# Revit family: CVSL-WM
name_source: partatom
category: Lighting Fixtures
revit_build: Autodesk Revit 2013 (Build: 20130531_2115(x64)
units: mm (PartAtom-declared; Revit-internal decimal feet)

## types (1)
- CVSL
    Apparent Load = 63 VA
    Assembly Code = D5020210
    Color Filter = 16777215
    Description = Curvista Wall Mount
    Dimming Lamp Color Temperature Shift = <None>
    Emit Shape Visible in Rendering = No
    Emit from Rectangle Length = 3 "
    Emit from Rectangle Width = 48 "
    Glass = Hubbell - White Glass
    Housing Material = Hubbell - White
    Lamp = T5, T5HO, T8
    Load Classification = Lighting
    Manufacturer = Alera Lighting
    Model = CVSLWM
    Photometric Notes = More IES files download on Photometric Web Link
    Photometric Web File = CVSL-2T8-WM-E.ies
    Photometric Web Link = https://www.hubbell.com
    Power Factor = 1
    Product Documentation Link = https://hubbellcdn.com
    Product Page URL = https://www.hubbell.com
    Row Option = CVSL : 4'
    Tilt Angle = 90.00°
    URL = https://www.hubbell.com
    Voltage = 120 V
    Watts = 63 W

## geometry (parser evidence)
native form markers: Blend x3, Sweep x5
no freeform markers — native parametric forms only
